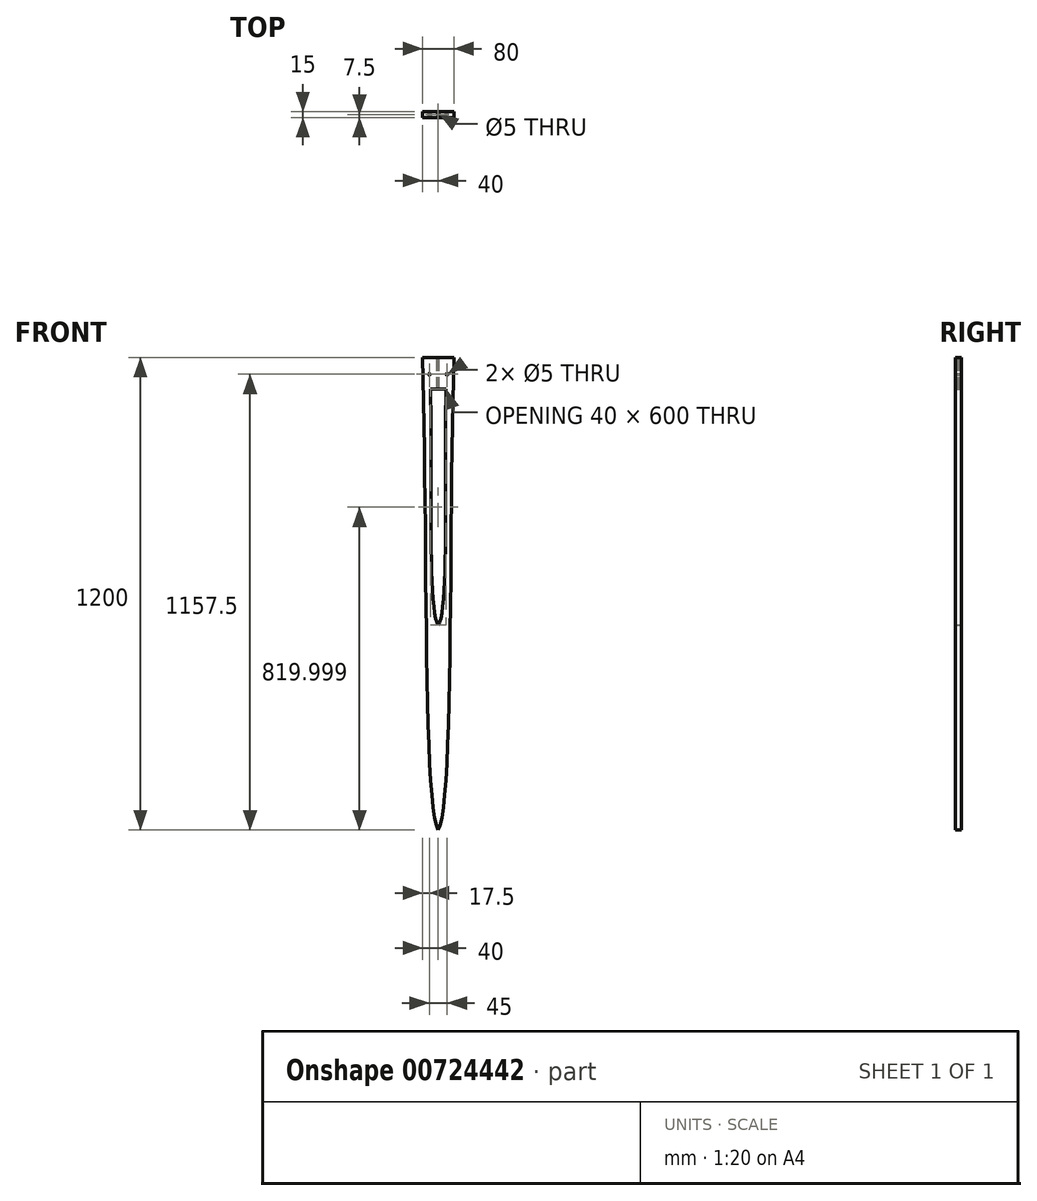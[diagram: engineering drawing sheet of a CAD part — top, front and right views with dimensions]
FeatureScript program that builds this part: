
annotation { "Feature Type Name" : "Feature", "Feature Type Description" : "" }
export const myFeature = defineFeature(function(context is Context, id is Id, definition is map)
    precondition{}
    {
        {
            var Q0;
            Q0=qCreatedBy(makeId("Front.planeOp"),FACE);
            var sketch = newSketch(context, id + "F0", { "sketchPlane" : qUnion([Q0])});
            skLineSegment(sketch, "E0.bottom", {"start": v(-60, 1254.42) * mm, "end": v(20, 1254.42) * mm});
            skLineSegment(sketch, "E1.bottom", {"start": v(-40, 1174.42) * mm, "end": v(0, 1174.42) * mm});
            skFitSpline(sketch, "E2", {"points": [v(0, 1174.42) * mm, v(-20, 574.42) * mm], "startDerivative": vector(-20, -600) * mm, "endDerivative": vector(-85.9, -119.76) * mm});
            skFitSpline(sketch, "E3.MirrorCS", {"points": [v(-40, 1174.42) * mm, v(-20, 574.42) * mm], "startDerivative": vector(20, -600) * mm, "endDerivative": vector(85.9, -119.76) * mm});
            skFitSpline(sketch, "E4", {"points": [v(20, 1254.42) * mm, v(-20, 54.42) * mm], "startDerivative": vector(-40, -1200) * mm, "endDerivative": vector(-120, -187.83) * mm});
            skFitSpline(sketch, "E5.MirrorCS", {"points": [v(-60, 1254.42) * mm, v(-20, 54.42) * mm], "startDerivative": vector(40, -1200) * mm, "endDerivative": vector(120, -187.83) * mm});
            skCircle(sketch, "E6", {"center": v(2.5, 1211.92) * mm, "radius": 2.5 * mm});
            skCircle(sketch, "E7.MirrorC", {"center": v(-42.5, 1211.92) * mm, "radius": 2.5 * mm});
            skSolve(sketch);
        }
        {
            var Q0;
            Q0=makeQuery(id+"F0.imprint","IMPRINT",FACE,{"disambiguationData":[TD([[makeQuery(id+"F0.imprint","IMPRINT",EDGE,{"derivedFrom":sQuery(id+"F0.wireOp",EDGE,"E0.bottom")}),-1.0]])]});
            extrude(context, id + "F1", {"entities" : qUnion([Q0]), "depth" : 15 * mm, "offsetDistance" : 25 * mm});
        }
        {
            var Q0;
            Q0=makeQuery(id+"F1.opExtrude","SWEPT_FACE",FACE,{"disambiguationData":[OSD([sQuery(id+"F0.wireOp",EDGE,"E0.bottom")])]});
            var sketch = newSketch(context, id + "F2", { "sketchPlane" : qUnion([Q0])});
            skCircle(sketch, "E8", {"center": v(-20, -7.5) * mm, "radius": 2.5 * mm});
            skSolve(sketch);
        }
        {
            var Q0;
            Q0=makeQuery(id+"F2.imprint","IMPRINT",FACE,{"disambiguationData":[TD([[makeQuery(id+"F2.imprint","IMPRINT",EDGE,{"derivedFrom":sQuery(id+"F2.wireOp",EDGE,"E8")}),1.0]])]});
            extrude(context, id + "F3", {"entities" : qUnion([Q0]), "operationType" : NewBodyOperationType.REMOVE, "oppositeDirection" : true, "depth" : 80 * mm, "offsetDistance" : 25 * mm});
        }
    });
